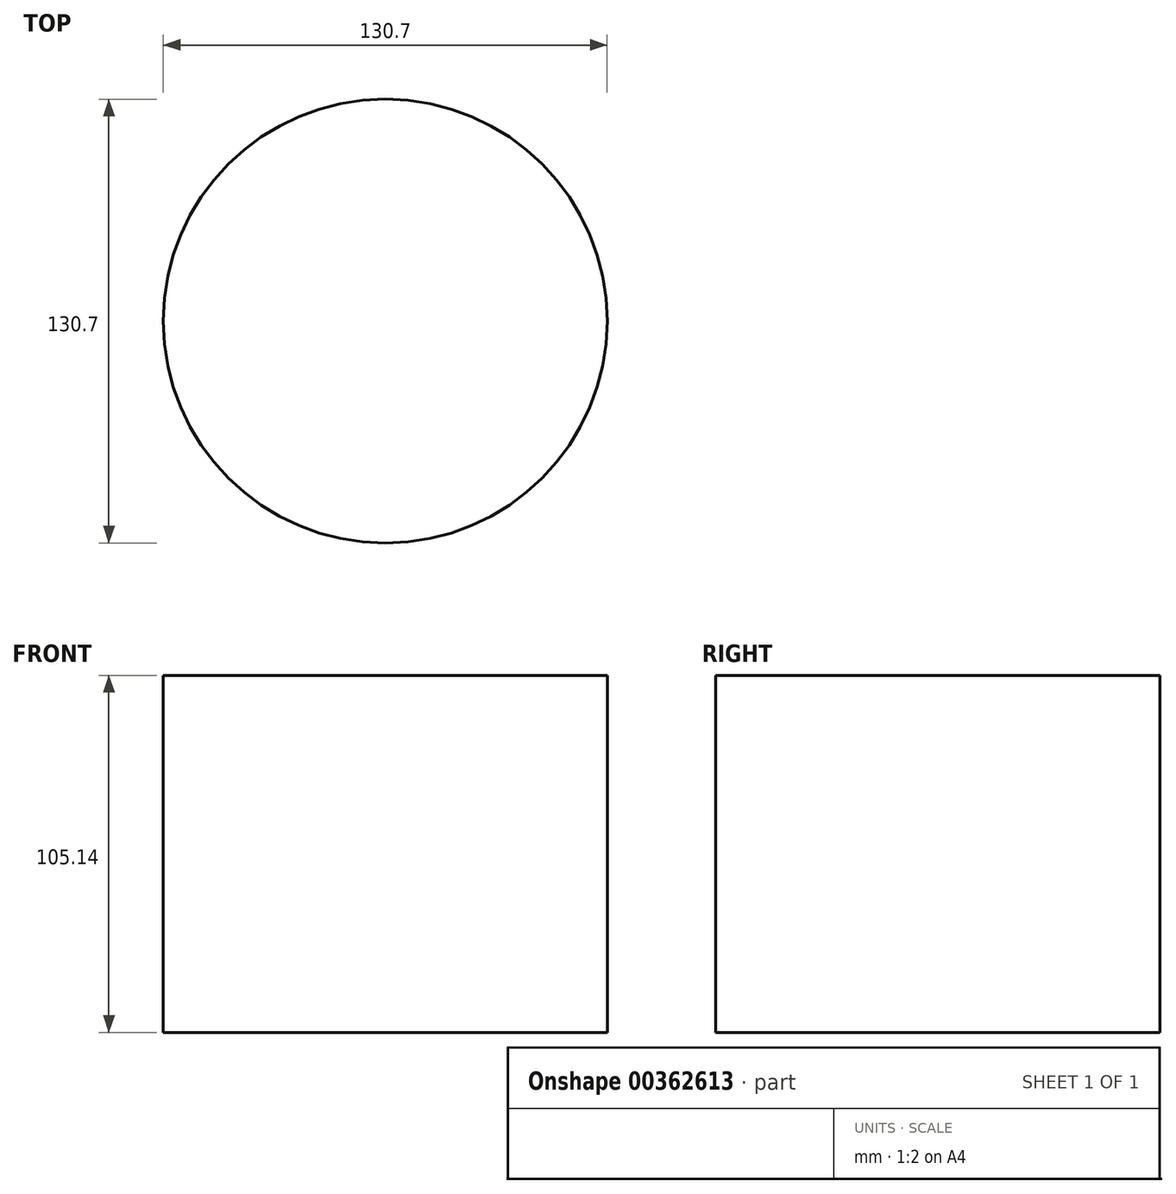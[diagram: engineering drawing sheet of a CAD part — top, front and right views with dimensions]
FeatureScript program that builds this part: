
annotation { "Feature Type Name" : "Feature", "Feature Type Description" : "" }
export const myFeature = defineFeature(function(context is Context, id is Id, definition is map)
    precondition{}
    {
        {
            var Q0;
            Q0=qCreatedBy(makeId("Top.planeOp"),FACE);
            var sketch = newSketch(context, id + "F0", { "sketchPlane" : qUnion([Q0])});
            skCircle(sketch, "E0", {"center": v(0, 0) * mm, "radius": 65.35 * mm});
            skSolve(sketch);
        }
        {
            var Q0;
            Q0 = qSketchRegion(id + "F0", true);
            extrude(context, id + "F1", {"entities" : qUnion([Q0]), "depth" : 105.14 * mm});
        }
    });
